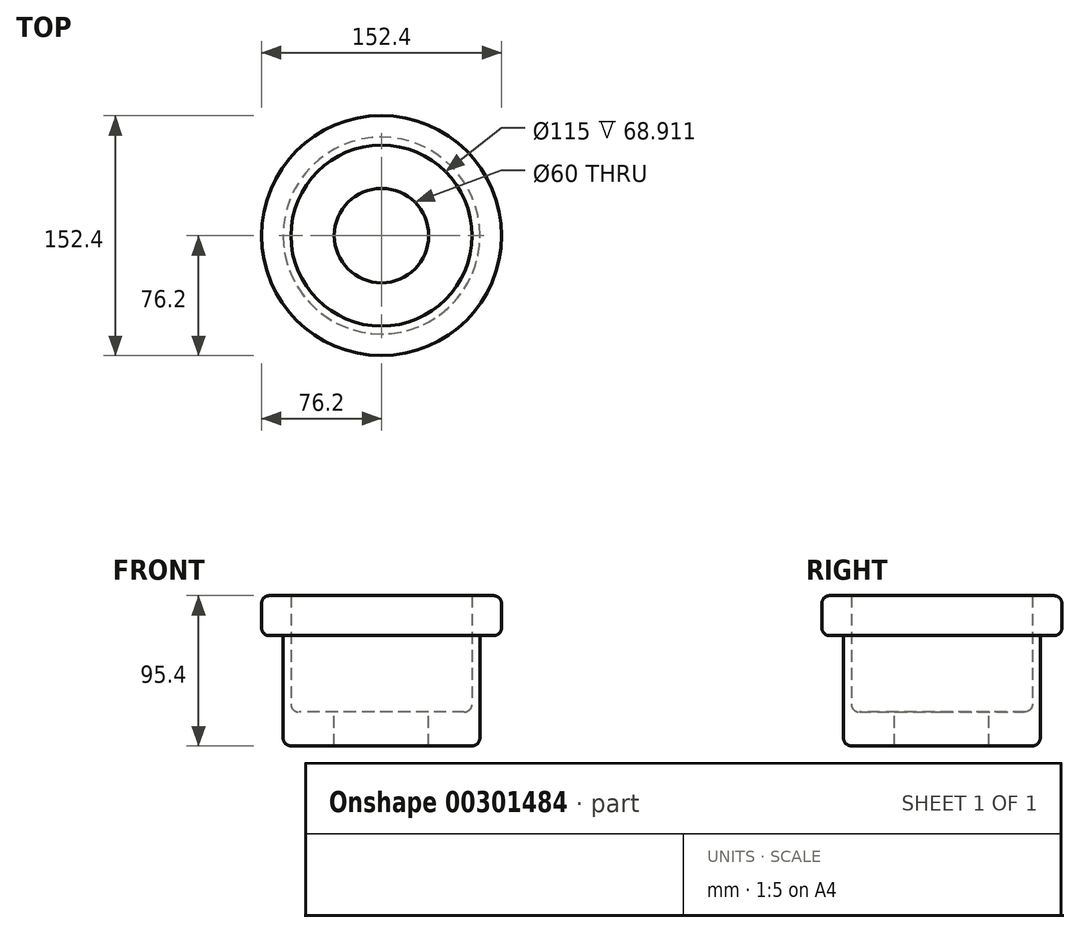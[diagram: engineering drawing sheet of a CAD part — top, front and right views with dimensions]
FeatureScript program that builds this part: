
annotation { "Feature Type Name" : "Feature", "Feature Type Description" : "" }
export const myFeature = defineFeature(function(context is Context, id is Id, definition is map)
    precondition{}
    {
        {
            var Q0;
            Q0=qCreatedBy(makeId("Front.planeOp"),FACE);
            var sketch = newSketch(context, id + "F0", { "sketchPlane" : qUnion([Q0])});
            skLineSegment(sketch, "E0", {"start": v(0, 48.51) * mm, "end": v(0, -21.49) * mm});
            skLineSegment(sketch, "E1", {"start": v(-76.2, 48.51) * mm, "end": v(0, 48.51) * mm});
            skLineSegment(sketch, "E2", {"start": v(-76.2, 48.51) * mm, "end": v(-76.2, 73.91) * mm});
            skLineSegment(sketch, "E3", {"start": v(-76.2, 73.91) * mm, "end": v(0, 73.91) * mm});
            skLineSegment(sketch, "E4", {"start": v(0, 73.91) * mm, "end": v(0, 48.51) * mm});
            skLineSegment(sketch, "E5", {"start": v(-62.5, 48.51) * mm, "end": v(-62.5, -21.49) * mm});
            skLineSegment(sketch, "E6", {"start": v(-62.5, -21.49) * mm, "end": v(0, -21.49) * mm});
            skSolve(sketch);
        }
        {
            var Q0;
            Q0=qCreatedBy(makeId("Top.planeOp"),FACE);
            var sketch = newSketch(context, id + "F1", { "sketchPlane" : qUnion([Q0])});
            skCircle(sketch, "E7", {"center": v(0, 0) * mm, "radius": 57.5 * mm});
            skSolve(sketch);
        }
        {
            var Q0;
            Q0 = qSketchRegion(id + "F0", true);
            var Q1;
            Q1=sQuery(id+"F0.wireOp",EDGE,"E4");
            revolve(context, id + "F2", {"entities" : qUnion([Q0]), "axis" : qUnion([Q1]), "revolveType" : RevolveType.FULL});
        }
        {
            var Q0;
            Q0 = qSketchRegion(id + "F1", true);
            var Q1;
            Q1=makeQuery(id+"F2.opRevolve","SWEPT_FACE",FACE,{"disambiguationData":[OSD([sQuery(id+"F0.wireOp",EDGE,"E3")])]});
            var Q2;
            Q2=makeQuery(id+"F2.opRevolve","SWEPT_BODY",BODY,{"disambiguationData":[OSD([sQuery(id+"F0.wireOp",EDGE,"E0"),sQuery(id+"F0.wireOp",EDGE,"E1"),sQuery(id+"F0.wireOp",EDGE,"E2"),sQuery(id+"F0.wireOp",EDGE,"E3"),sQuery(id+"F0.wireOp",EDGE,"E4"),sQuery(id+"F0.wireOp",EDGE,"E5"),sQuery(id+"F0.wireOp",EDGE,"E6")])]});
            extrude(context, id + "F3", {"entities" : qUnion([Q0]), "operationType" : NewBodyOperationType.REMOVE, "endBound" : BoundingType.UP_TO_BODY, "endBoundEntityFace" : qUnion([Q1]), "endBoundEntityBody" : qUnion([Q2]), "depth" : 25 * mm});
        }
        {
            var Q0;
            Q0=qCreatedBy(makeId("Top.planeOp"),FACE);
            var sketch = newSketch(context, id + "F4", { "sketchPlane" : qUnion([Q0])});
            skCircle(sketch, "E8", {"center": v(0, 0) * mm, "radius": 30 * mm});
            skSolve(sketch);
        }
        {
            var Q0;
            Q0=makeQuery(id+"F4.imprint","IMPRINT",FACE,{"disambiguationData":[TD([[makeQuery(id+"F4.imprint","IMPRINT",EDGE,{"derivedFrom":sQuery(id+"F4.wireOp",EDGE,"E8")}),1.0]])]});
            extrude(context, id + "F5", {"entities" : qUnion([Q0]), "operationType" : NewBodyOperationType.REMOVE, "endBound" : BoundingType.THROUGH_ALL, "oppositeDirection" : true, "depth" : 25 * mm});
        }
        {
            var Q0;
            Q0=makeQuery(id+"F3.boolean.opBoolean","COPY",EDGE,{"derivedFrom":makeQuery(id+"F3.opExtrude","CAP_EDGE",EDGE,{"disambiguationData":[OSD([sQuery(id+"F1.wireOp",EDGE,"E7")])],"isStart":false})});
            var Q1;
            Q1=makeQuery(id+"F2.opRevolve","SWEPT_EDGE",EDGE,{"disambiguationData":[OSD([sQuery(id+"F0.wireOp",EDGE,"E2"),sQuery(id+"F0.wireOp",EDGE,"E3")])]});
            var Q2;
            Q2=makeQuery(id+"F2.opRevolve","SWEPT_EDGE",EDGE,{"disambiguationData":[OSD([sQuery(id+"F0.wireOp",EDGE,"E1"),sQuery(id+"F0.wireOp",EDGE,"E2")])]});
            var Q3;
            Q3=makeQuery(id+"F2.opRevolve","SWEPT_EDGE",EDGE,{"disambiguationData":[OSD([sQuery(id+"F0.wireOp",EDGE,"E5"),sQuery(id+"F0.wireOp",EDGE,"E6")])]});
            var Q4;
            Q4=makeQuery(id+"F5.boolean.opBoolean","COPY",EDGE,{"derivedFrom":makeQuery(id+"F5.opExtrude","CAP_EDGE",EDGE,{"disambiguationData":[OSD([sQuery(id+"F4.wireOp",EDGE,"E8")])],"isStart":true})});
            var Q5;
            Q5=makeQuery(id+"F3.boolean.opBoolean","COPY",EDGE,{"derivedFrom":makeQuery(id+"F3.opExtrude","CAP_EDGE",EDGE,{"disambiguationData":[OSD([sQuery(id+"F1.wireOp",EDGE,"E7")])],"isStart":true})});
            fillet(context, id + "F6", {"entities" : qUnion([Q0, Q1, Q2, Q3, Q4, Q5]), "radius" : 5 * mm, "tangentPropagation" : true, "allowEdgeOverflow" : false});
        }
    });
